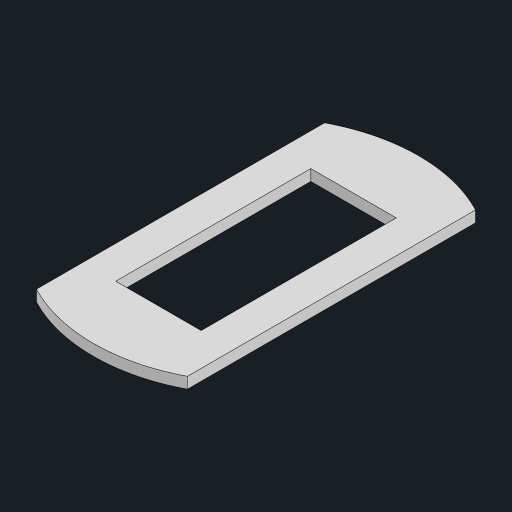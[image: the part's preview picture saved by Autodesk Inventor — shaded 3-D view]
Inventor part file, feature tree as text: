
AUTODESK INVENTOR PART (.ipt)
format: ipt  version: 2023 (Build 270158000, 158)  size: 96,256 bytes
history: native  units: mm
features: other x1, extrude x1, sketch x1
ambient origin geometry x8: Origin, YZ Plane, XZ Plane, XY Plane, X Axis, Y Axis, Z Axis, Center Point
bodies: Body1 (feature_tree)
feature tree (3):
  other  "ソリッド1"
  extrude  "押し出し1"  Depth=35.0mm
  sketch  "スケッチ1"
